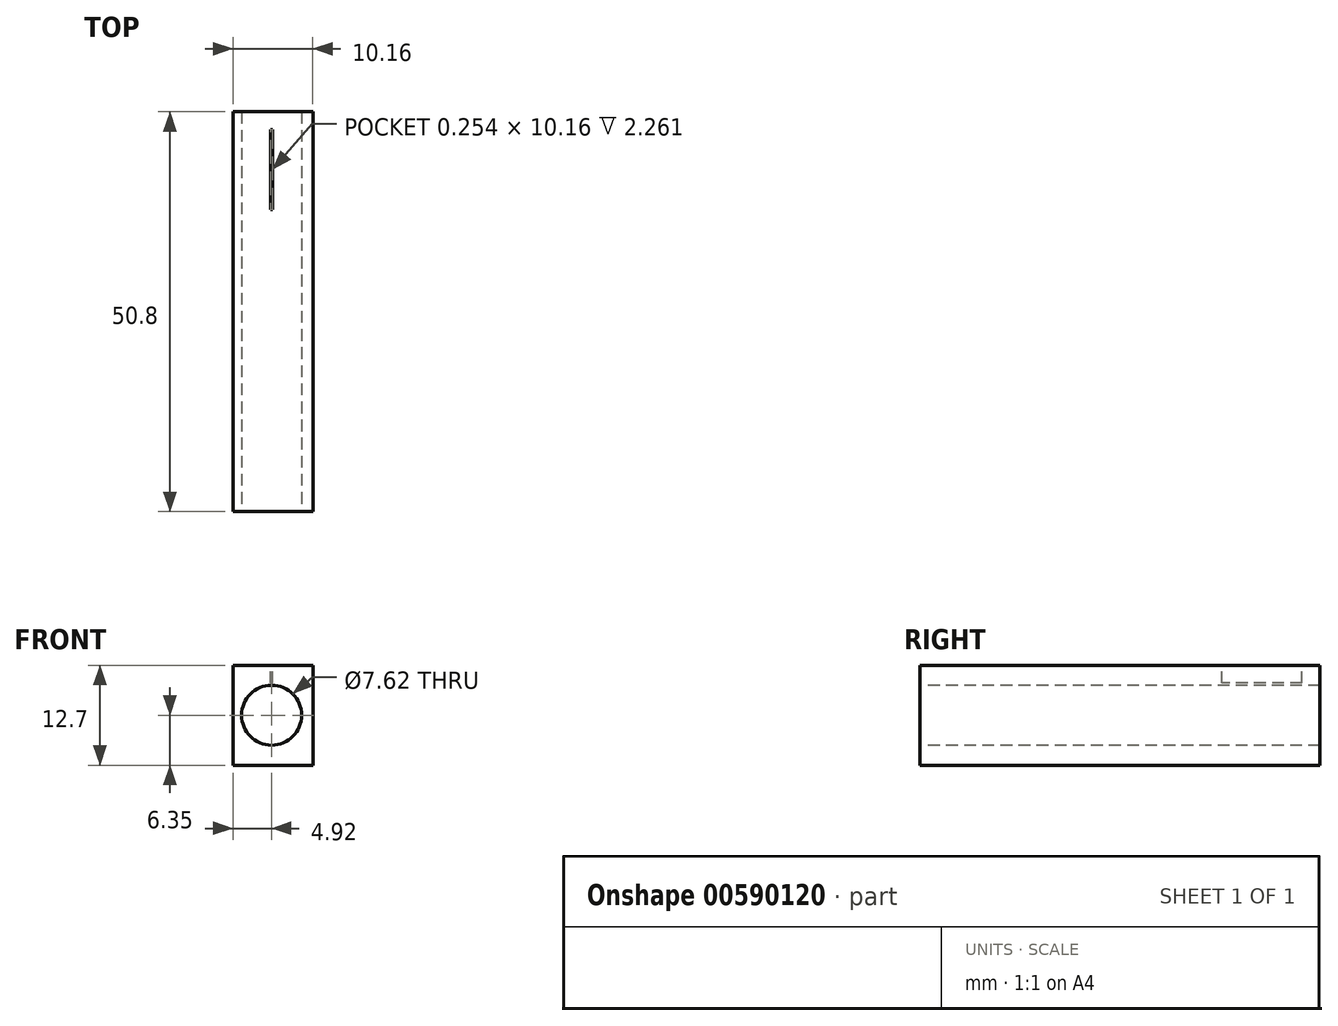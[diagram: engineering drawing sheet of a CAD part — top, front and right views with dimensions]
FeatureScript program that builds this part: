
annotation { "Feature Type Name" : "Feature", "Feature Type Description" : "" }
export const myFeature = defineFeature(function(context is Context, id is Id, definition is map)
    precondition{}
    {
        {
            var Q0;
            Q0=qCreatedBy(makeId("Front.planeOp"),FACE);
            var sketch = newSketch(context, id + "F0", { "sketchPlane" : qUnion([Q0])});
            skLineSegment(sketch, "E0", {"start": v(-31.83, 23.33) * mm, "end": v(-31.83, 10.63) * mm});
            skLineSegment(sketch, "E1", {"start": v(-31.83, 10.63) * mm, "end": v(-21.67, 10.63) * mm});
            skLineSegment(sketch, "E2", {"start": v(-21.67, 10.63) * mm, "end": v(-21.67, 23.33) * mm});
            skLineSegment(sketch, "E3", {"start": v(-31.83, 23.33) * mm, "end": v(-21.67, 23.33) * mm});
            skSolve(sketch);
        }
        {
            var Q0;
            Q0 = qSketchRegion(id + "F0", true);
            extrude(context, id + "F1", {"entities" : qUnion([Q0]), "depth" : 50.8 * mm, "offsetDistance" : 25.4 * mm});
        }
        {
            var Q0;
            Q0=makeQuery(id+"F1.opExtrude","CAP_FACE",FACE,{"disambiguationData":[OSD([sQuery(id+"F0.wireOp",EDGE,"E0"),sQuery(id+"F0.wireOp",EDGE,"E1"),sQuery(id+"F0.wireOp",EDGE,"E2"),sQuery(id+"F0.wireOp",EDGE,"E3")])],"isStart":false});
            var sketch = newSketch(context, id + "F2", { "sketchPlane" : qUnion([Q0])});
            skCircle(sketch, "E4", {"center": v(-26.9, 16.98) * mm, "radius": 3.81 * mm});
            skSolve(sketch);
        }
        {
            var Q0;
            Q0 = qSketchRegion(id + "F2", true);
            extrude(context, id + "F3", {"entities" : qUnion([Q0]), "operationType" : NewBodyOperationType.REMOVE, "oppositeDirection" : true, "depth" : 76.2 * mm, "offsetDistance" : 25.4 * mm});
        }
        {
            var Q0;
            Q0=makeQuery(id+"F1.opExtrude","SWEPT_FACE",FACE,{"disambiguationData":[OSD([sQuery(id+"F0.wireOp",EDGE,"E3")])]});
            var sketch = newSketch(context, id + "F4", { "sketchPlane" : qUnion([Q0])});
            skLineSegment(sketch, "E5", {"start": v(-27.01, -12.44) * mm, "end": v(-26.76, -12.44) * mm});
            skLineSegment(sketch, "E6", {"start": v(-26.76, -12.44) * mm, "end": v(-26.76, -2.28) * mm});
            skLineSegment(sketch, "E7", {"start": v(-27.01, -2.28) * mm, "end": v(-27.01, -12.44) * mm});
            skLineSegment(sketch, "E8", {"start": v(-27.01, -2.28) * mm, "end": v(-26.76, -2.28) * mm});
            skSolve(sketch);
        }
        {
            var Q0;
            Q0 = qSketchRegion(id + "F4", true);
            extrude(context, id + "F5", {"entities" : qUnion([Q0]), "operationType" : NewBodyOperationType.REMOVE, "oppositeDirection" : true, "depth" : 2.26 * mm, "offsetDistance" : 25.4 * mm});
        }
    });
